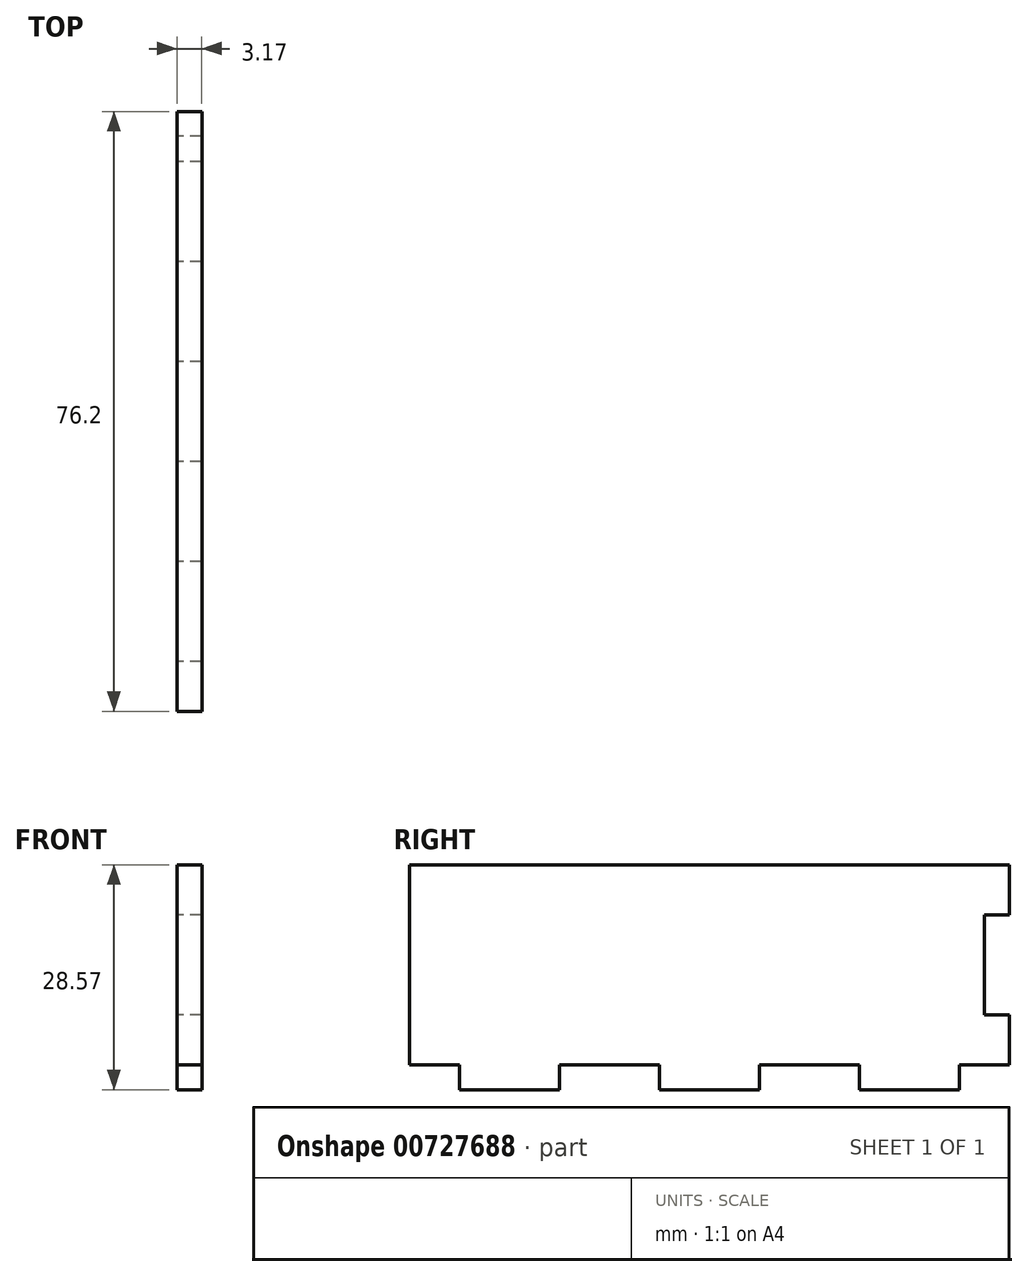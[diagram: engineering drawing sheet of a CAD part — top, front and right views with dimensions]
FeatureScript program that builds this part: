
annotation { "Feature Type Name" : "Feature", "Feature Type Description" : "" }
export const myFeature = defineFeature(function(context is Context, id is Id, definition is map)
    precondition{}
    {
        {
            var Q0;
            Q0=qCreatedBy(makeId("Right.planeOp"),FACE);
            var sketch = newSketch(context, id + "F0", { "sketchPlane" : qUnion([Q0])});
            skLineSegment(sketch, "E0", {"start": v(0, 0) * mm, "end": v(-63.5, 0) * mm});
            skLineSegment(sketch, "E1", {"start": v(-63.5, 0) * mm, "end": v(-63.5, 3.17) * mm});
            skLineSegment(sketch, "E2", {"start": v(-63.5, 3.17) * mm, "end": v(-69.85, 3.17) * mm});
            skLineSegment(sketch, "E3", {"start": v(0, 0) * mm, "end": v(0, 3.18) * mm});
            skLineSegment(sketch, "E4", {"start": v(0, 3.18) * mm, "end": v(6.35, 3.18) * mm});
            skLineSegment(sketch, "E5", {"start": v(6.35, 3.18) * mm, "end": v(6.35, 28.58) * mm});
            skLineSegment(sketch, "E6", {"start": v(6.35, 28.58) * mm, "end": v(-69.85, 28.58) * mm});
            skLineSegment(sketch, "E7", {"start": v(-69.85, 28.58) * mm, "end": v(-69.85, 3.17) * mm});
            skLineSegment(sketch, "E8", {"start": v(-63.5, 0) * mm, "end": v(-50.8, 0) * mm});
            skLineSegment(sketch, "E9", {"start": v(-50.8, 0) * mm, "end": v(-50.8, 3.17) * mm});
            skLineSegment(sketch, "E10", {"start": v(-50.8, 3.17) * mm, "end": v(-38.1, 3.17) * mm});
            skLineSegment(sketch, "E11", {"start": v(-38.1, 3.17) * mm, "end": v(-38.1, 0) * mm});
            skLineSegment(sketch, "E12", {"start": v(-38.1, 0) * mm, "end": v(-25.4, 0) * mm});
            skLineSegment(sketch, "E13", {"start": v(-25.4, 0) * mm, "end": v(-25.4, 3.17) * mm});
            skLineSegment(sketch, "E14", {"start": v(-25.4, 3.17) * mm, "end": v(-12.7, 3.17) * mm});
            skLineSegment(sketch, "E15", {"start": v(-12.7, 3.17) * mm, "end": v(-12.7, 0) * mm});
            skLineSegment(sketch, "E16", {"start": v(6.35, 28.58) * mm, "end": v(6.35, 22.23) * mm});
            skLineSegment(sketch, "E17", {"start": v(6.35, 22.23) * mm, "end": v(3.18, 22.23) * mm});
            skLineSegment(sketch, "E18", {"start": v(3.18, 22.23) * mm, "end": v(3.18, 9.53) * mm});
            skLineSegment(sketch, "E19", {"start": v(3.18, 9.53) * mm, "end": v(6.35, 9.53) * mm});
            skSolve(sketch);
        }
        {
            var Q0;
            Q0=makeQuery(id+"F0.imprint","IMPRINT",FACE,{"disambiguationData":[TD([[makeQuery(id+"F0.imprint","IMPRINT",EDGE,{"derivedFrom":sQuery(id+"F0.wireOp",EDGE,"E1")}),-1.0]])]});
            extrude(context, id + "F1", {"entities" : qUnion([Q0]), "depth" : 3.17 * mm, "offsetDistance" : 25.4 * mm});
        }
    });
